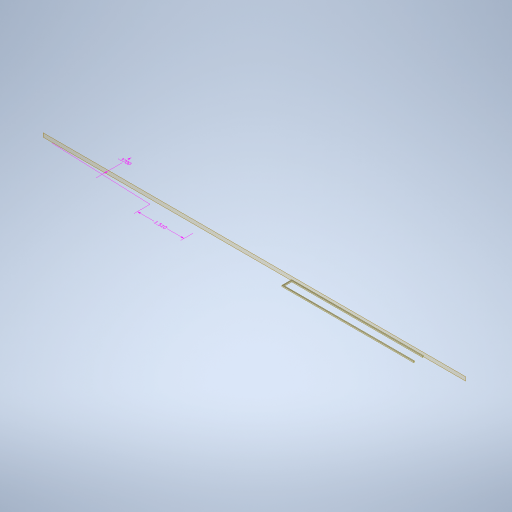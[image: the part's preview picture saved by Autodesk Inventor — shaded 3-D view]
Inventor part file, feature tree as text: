
AUTODESK INVENTOR PART (.ipt)
format: ipt  version: 2024.2 (Build 282272000, 272)  size: 275,456 bytes
history: native  units: in
note: dims shown in document units (in); Inventor stores cm internally (conversion verified against a paired STEP export)
features: other x3, plane x3, sketch x2, sweep x1
ambient origin geometry x8: Origin, YZ Plane, XZ Plane, XY Plane, X Axis, Y Axis, Z Axis, Center Point
bodies: Solid1 (feature_tree)
feature tree (9):
  other  "Annotations"
  sweep  "Sweep1"
  plane  "Work Plane1"
  plane  "Work Plane2"
  plane  "Work Plane4"
  sketch  "Sketch1"  dims[d6=0.0in d7=0.0in d11=0.25in d19=-0.25in]
  sketch  "Sketch2"  dims[d69=1.325in d70=1.325in d86=-0.1175in d89=0.1in d90=0.0in d91=0.0in d92=0.0in d98=0.01in d99=0.01in d42=0.2341in d43=0.169in d44=0.37in d48=0.2141in d49=0.2512in d50=1.51in]
  other  "Linear Dimension 1"
  other  "Linear Dimension 3"
